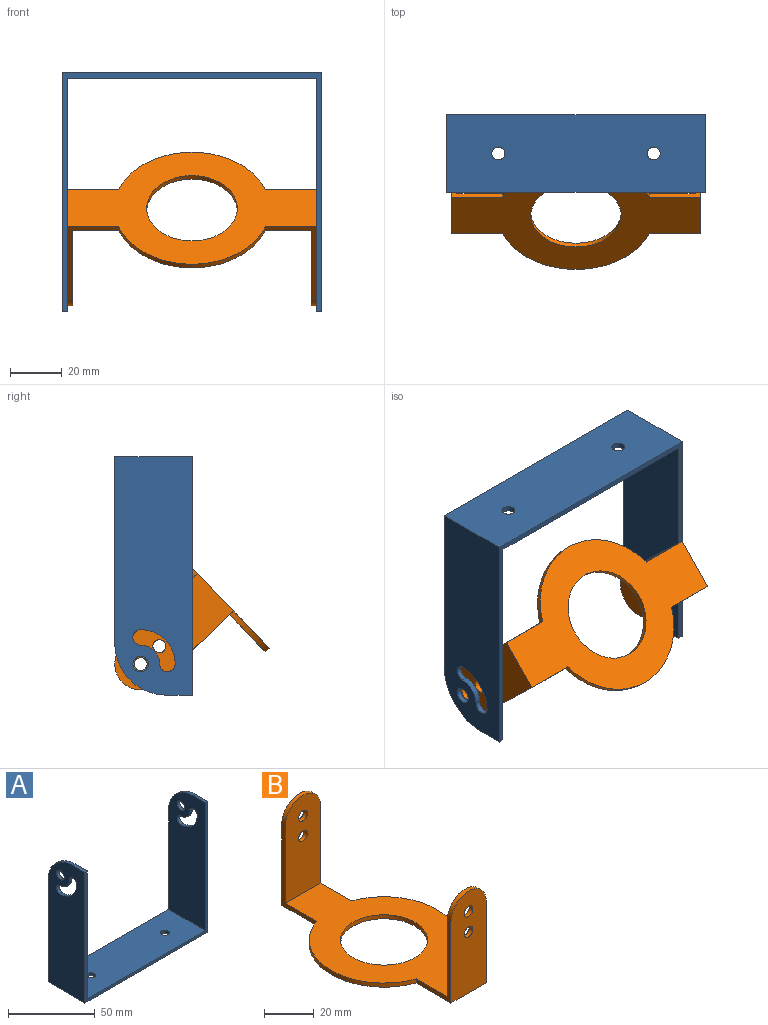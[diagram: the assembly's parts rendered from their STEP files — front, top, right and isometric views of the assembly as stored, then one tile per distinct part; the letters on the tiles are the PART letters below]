
ASSEMBLY  parts=2 mates=1
PART A: 24 faces, bbox 100x30x92 mm
  f0: plane 96x30mm, normal (0,0,1), area 2840.7mm2, adj f2,f4,f6,f8,f12,f13
  f1: plane 92x30mm, normal (-1,0,0), area 2520.4mm2, adj f2,f4,f5,f7,f11,f15,f20,f21
  f2: plane 100x92mm, normal (0,-1,0), area 560mm2, adj f0,f1,f3,f5,f6,f7,f8,f9
  f3: plane 92x30mm, normal (1,0,0), area 2520.4mm2, adj f2,f4,f5,f9,f10,f14,f16,f17
  f4: plane 100x72mm, normal (0,1,0), area 480mm2, adj f0,f1,f3,f5,f6,f8,f10,f11
  f5: plane 100x30mm, normal (0,0,-1), area 2960.7mm2, adj f1,f2,f3,f4,f12,f13
  f6: plane 90x30mm, normal (1,0,0), area 2460.4mm2, adj f0,f2,f4,f7,f11,f15,f20,f21
  f7: plane 10x2mm, normal (0,0,1), area 20mm2, adj f1,f2,f6,f11
  f8: plane 90x30mm, normal (-1,0,0), area 2460.4mm2, adj f0,f2,f4,f9,f10,f14,f16,f17
  f9: plane 10x2mm, normal (0,0,1), area 20mm2, adj f2,f3,f8,f10
  f10: cylinder r=20mm len=20mm, axis (1,0,0), area 62.8mm2, adj f3,f4,f8,f9
  f11: cylinder r=20mm len=20mm, axis (1,0,0), area 62.8mm2, adj f1,f4,f6,f7
  f12: cylinder r=2.5mm len=5mm, axis (0,0,-1), area 31.4mm2, adj f0,f5
  f13: cylinder r=2.5mm len=5mm, axis (0,0,-1), area 31.4mm2, adj f0,f5
  f14: cylinder r=3mm len=6mm, axis (1,0,0), area 37.7mm2, adj f3,f8
  f15: cylinder r=3mm len=6mm, axis (1,0,0), area 37.7mm2, adj f1,f6
  f16: cylinder r=3mm len=6mm, axis (1,0,0), area 18.8mm2, adj f3,f8,f17,f19
  f17: cylinder r=13.31mm len=13.31mm, axis (1,0,0), area 41.8mm2, adj f3,f8,f16,f18
  f18: cylinder r=3mm len=6mm, axis (1,0,0), area 18.8mm2, adj f3,f8,f17,f19
  f19: cylinder r=7.31mm len=7.31mm, axis (1,0,0), area 23mm2, adj f3,f8,f16,f18
  f20: cylinder r=7.31mm len=7.31mm, axis (1,0,0), area 23mm2, adj f1,f6,f21,f23
  f21: cylinder r=3mm len=6mm, axis (1,0,0), area 18.8mm2, adj f1,f6,f20,f22
  f22: cylinder r=13.31mm len=13.31mm, axis (1,0,0), area 41.8mm2, adj f1,f6,f21,f23
  f23: cylinder r=3mm len=6mm, axis (1,0,0), area 18.8mm2, adj f1,f6,f20,f22
PART B: 19 faces, bbox 60x96x50 mm
  f0: plane 92x60mm, normal (0,0,1), area 2527.9mm2, adj f1,f2,f3,f5,f6,f7,f10,f11
  f1: plane 40x19.72mm, normal (-1,0,0), area 115.4mm2, adj f0,f2,f8,f9,f11,f12
  f2: cylinder r=30mm len=56.57mm, axis (0,0,-1), area 147.7mm2, adj f0,f1,f3,f9
  f3: plane 40x19.72mm, normal (-1,0,0), area 115.4mm2, adj f0,f2,f4,f9,f15,f16
  f4: plane 50x20mm, normal (0,-1,0), area 917.8mm2, adj f3,f5,f9,f16,f17,f18
  f5: plane 40x19.72mm, normal (1,0,0), area 115.4mm2, adj f0,f4,f6,f9,f15,f16
  f6: cylinder r=30mm len=56.57mm, axis (0,0,-1), area 147.7mm2, adj f0,f5,f7,f9
  f7: plane 40x19.72mm, normal (1,0,0), area 115.4mm2, adj f0,f6,f8,f9,f11,f12
  f8: plane 50x20mm, normal (0,1,0), area 917.8mm2, adj f1,f7,f9,f12,f13,f14
  f9: plane 96x60mm, normal (0,0,-1), area 2607.9mm2, adj f1,f2,f3,f4,f5,f6,f7,f8
  f10: cylinder r=17.5mm len=35mm, axis (0,0,-1), area 219.9mm2, adj f0,f9
  f11: plane 48x20mm, normal (0,-1,0), area 877.8mm2, adj f0,f1,f7,f12,f13,f14
  f12: cylinder r=10mm len=20mm, axis (0,1,0), area 62.8mm2, adj f1,f7,f8,f11
  f13: cylinder r=2.5mm len=5mm, axis (0,1,0), area 31.4mm2, adj f8,f11
  f14: cylinder r=2.5mm len=5mm, axis (0,1,0), area 31.4mm2, adj f8,f11
  f15: plane 48x20mm, normal (0,1,0), area 877.8mm2, adj f0,f3,f5,f16,f17,f18
  f16: cylinder r=10mm len=20mm, axis (0,-1,0), area 62.8mm2, adj f3,f4,f5,f15
  f17: cylinder r=2.5mm len=5mm, axis (0,-1,0), area 31.4mm2, adj f4,f15
  f18: cylinder r=2.5mm len=5mm, axis (0,-1,0), area 31.4mm2, adj f4,f15
PLACE A rot(axis=(0,-1,0),180deg) t=(83.24,6.3,200.33)mm fixed
PLACE B rot(axis=(-0.68,-0.68,-0.29),147.8deg) t=(33.24,-2.54,148.05)mm
MATE revolute B.f13 <-> A.f14  axis (-1,0,0) through (-14.76,26.3,120.33)mm
